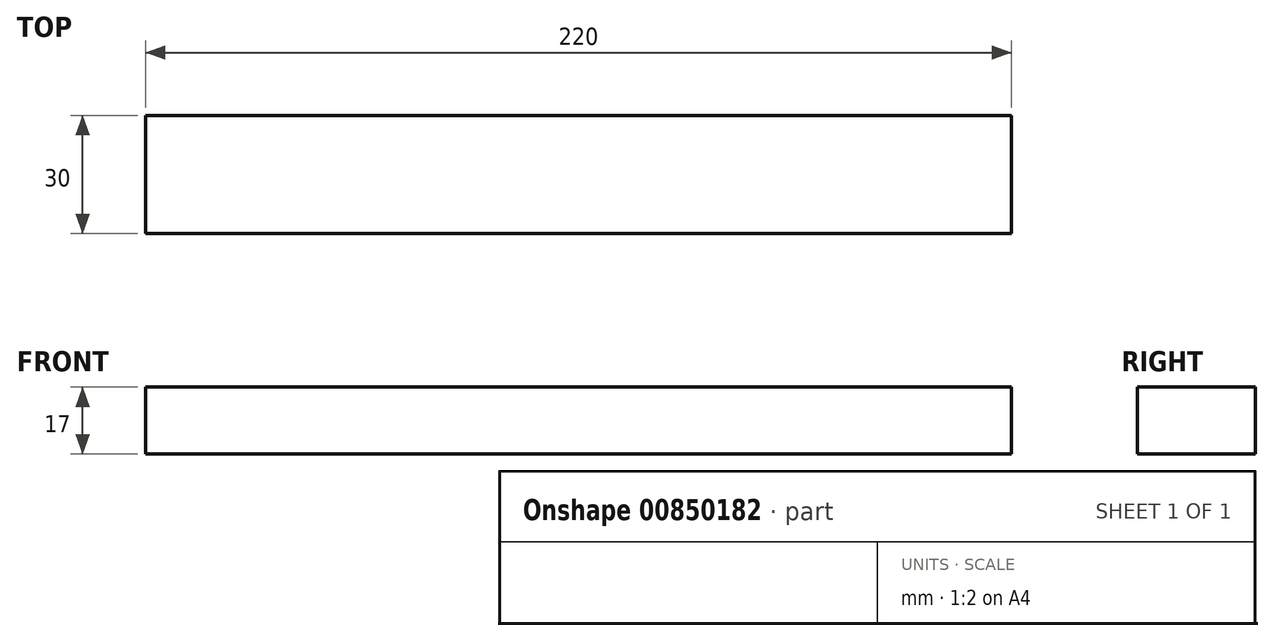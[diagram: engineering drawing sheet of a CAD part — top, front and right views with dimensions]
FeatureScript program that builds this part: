
annotation { "Feature Type Name" : "Feature", "Feature Type Description" : "" }
export const myFeature = defineFeature(function(context is Context, id is Id, definition is map)
    precondition{}
    {
        {
            var Q0;
            Q0=qCreatedBy(makeId("Right.planeOp"),FACE);
            var sketch = newSketch(context, id + "F0", { "sketchPlane" : qUnion([Q0])});
            skLineSegment(sketch, "E0.bottom", {"start": v(-15, 8.5) * mm, "end": v(15, 8.5) * mm});
            skLineSegment(sketch, "E0.top", {"start": v(-15, -8.5) * mm, "end": v(15, -8.5) * mm});
            skLineSegment(sketch, "E0.left", {"start": v(-15, 8.5) * mm, "end": v(-15, -8.5) * mm});
            skLineSegment(sketch, "E0.right", {"start": v(15, 8.5) * mm, "end": v(15, -8.5) * mm});
            skSolve(sketch);
        }
        {
            var Q0;
            Q0=qSketchRegion(id+"F0",true);
            extrude(context, id + "F1", {"entities" : qUnion([Q0]), "depth" : 220 * mm, "offsetDistance" : 25 * mm});
        }
    });
